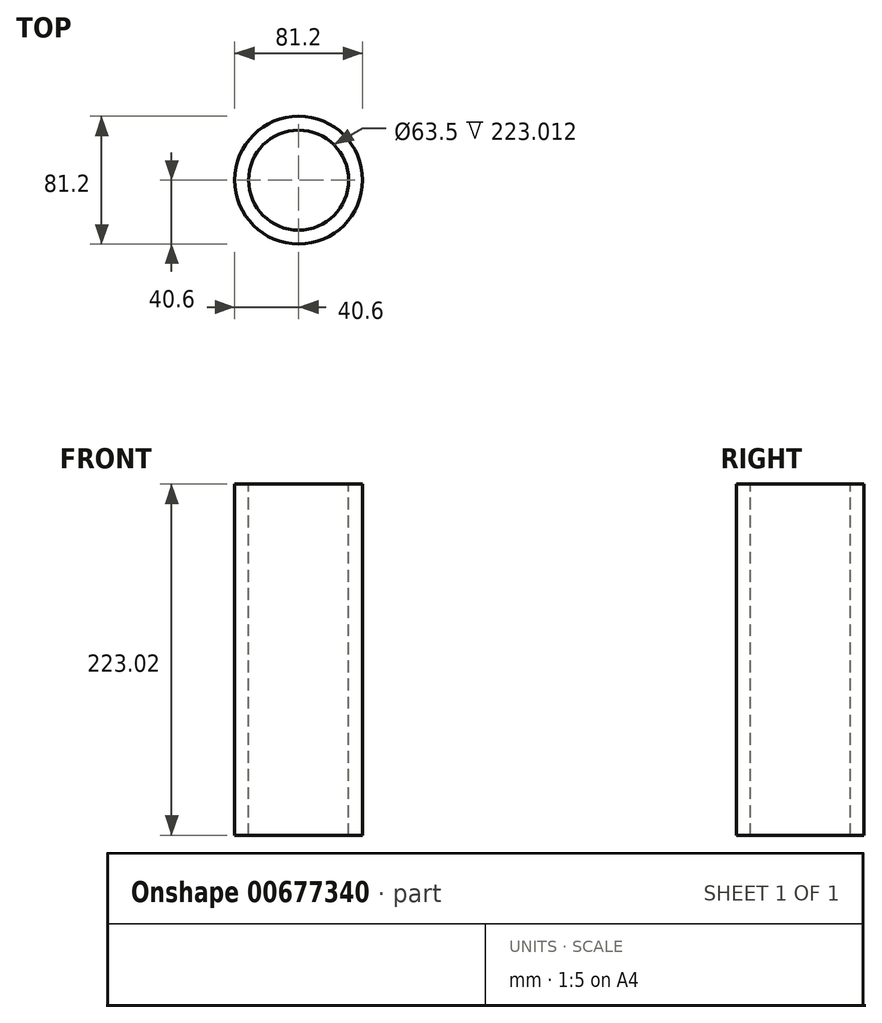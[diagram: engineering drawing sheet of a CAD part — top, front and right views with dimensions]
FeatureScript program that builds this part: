
annotation { "Feature Type Name" : "Feature", "Feature Type Description" : "" }
export const myFeature = defineFeature(function(context is Context, id is Id, definition is map)
    precondition{}
    {
        {
            var Q0;
            Q0=qCreatedBy(makeId("Top.planeOp"),FACE);
            var sketch = newSketch(context, id + "F0", { "sketchPlane" : qUnion([Q0])});
            skCircle(sketch, "E0", {"center": v(0, 0) * mm, "radius": 40.6 * mm});
            skSolve(sketch);
        }
        {
            var Q0;
            Q0=makeQuery(id+"F0.imprint","IMPRINT",FACE,{"disambiguationData":[TD([[makeQuery(id+"F0.imprint","IMPRINT",EDGE,{"derivedFrom":sQuery(id+"F0.wireOp",EDGE,"E0")}),1.0]])]});
            extrude(context, id + "F1", {"entities" : qUnion([Q0]), "endBound" : BoundingType.SYMMETRIC, "depth" : 223 * mm, "offsetDistance" : 25.4 * mm});
        }
        {
            var Q0;
            Q0=makeQuery(id+"F1.opExtrude","CAP_FACE",FACE,{"disambiguationData":[OSD([sQuery(id+"F0.wireOp",EDGE,"E0")])],"isStart":false});
            var sketch = newSketch(context, id + "F2", { "sketchPlane" : qUnion([Q0])});
            skPoint(sketch, "E1", {"position": v(0, 0) * mm});
            skSolve(sketch);
        }
        {
            var Q0;
            Q0=sQuery(id+"F2.wireOp",VERTEX,"E1");
            var Q1;
            Q1=makeQuery(id+"F1.opExtrude","SWEPT_BODY",BODY,{"disambiguationData":[OSD([sQuery(id+"F0.wireOp",EDGE,"E0")])]});
            hole(context, id + "F3", {"style" : HoleStyle.SIMPLE, "endStyle" : HoleEndStyle.THROUGH, "holeDiameter" : 63.5 * mm, "majorDiameter" : 6.35 * mm, "isTappedThrough" : true, "tappedDepth" : 12.7 * mm, "tapClearance" : 3, "locations" : qUnion([Q0]), "scope" : qUnion([Q1])});
        }
    });
